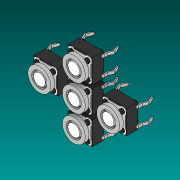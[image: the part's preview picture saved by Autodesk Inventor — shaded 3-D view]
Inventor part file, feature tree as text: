
AUTODESK INVENTOR PART (.ipt)
format: ipt  version: 2019 (Build 230136000, 136)  size: 973,824 bytes
history: native  units: mm
features: other x5, extrude x1, sketch x1
ambient origin geometry x8: Origin, YZ Plane, XZ Plane, XY Plane, X Axis, Y Axis, Z Axis, Center Point
bodies: Solid2 (feature_tree), Solid3 (feature_tree), Solid4 (feature_tree), Solid5 (feature_tree), Solid6 (feature_tree), Solid141 (feature_tree)
feature tree (7):
  extrude  "Extrusion1"  Depth=4.0mm
  sketch  "Sketch1"  dims[d0=4.0mm d1=4.0mm d2=4.0mm d3=4.0mm d4=4.0mm d5=1.0mm d6=1.0mm d7=1.0mm d8=1.0mm d9=1.0mm d10=1.0mm d11=0.0mm]
  other  "4301x60507x6_3:1"
  other  "4301x60507x6_5:1"
  other  "4301x60507x6_7:1"
  other  "4301x60507x6_9:1"
  other  "4301x60507x6_11:1"
